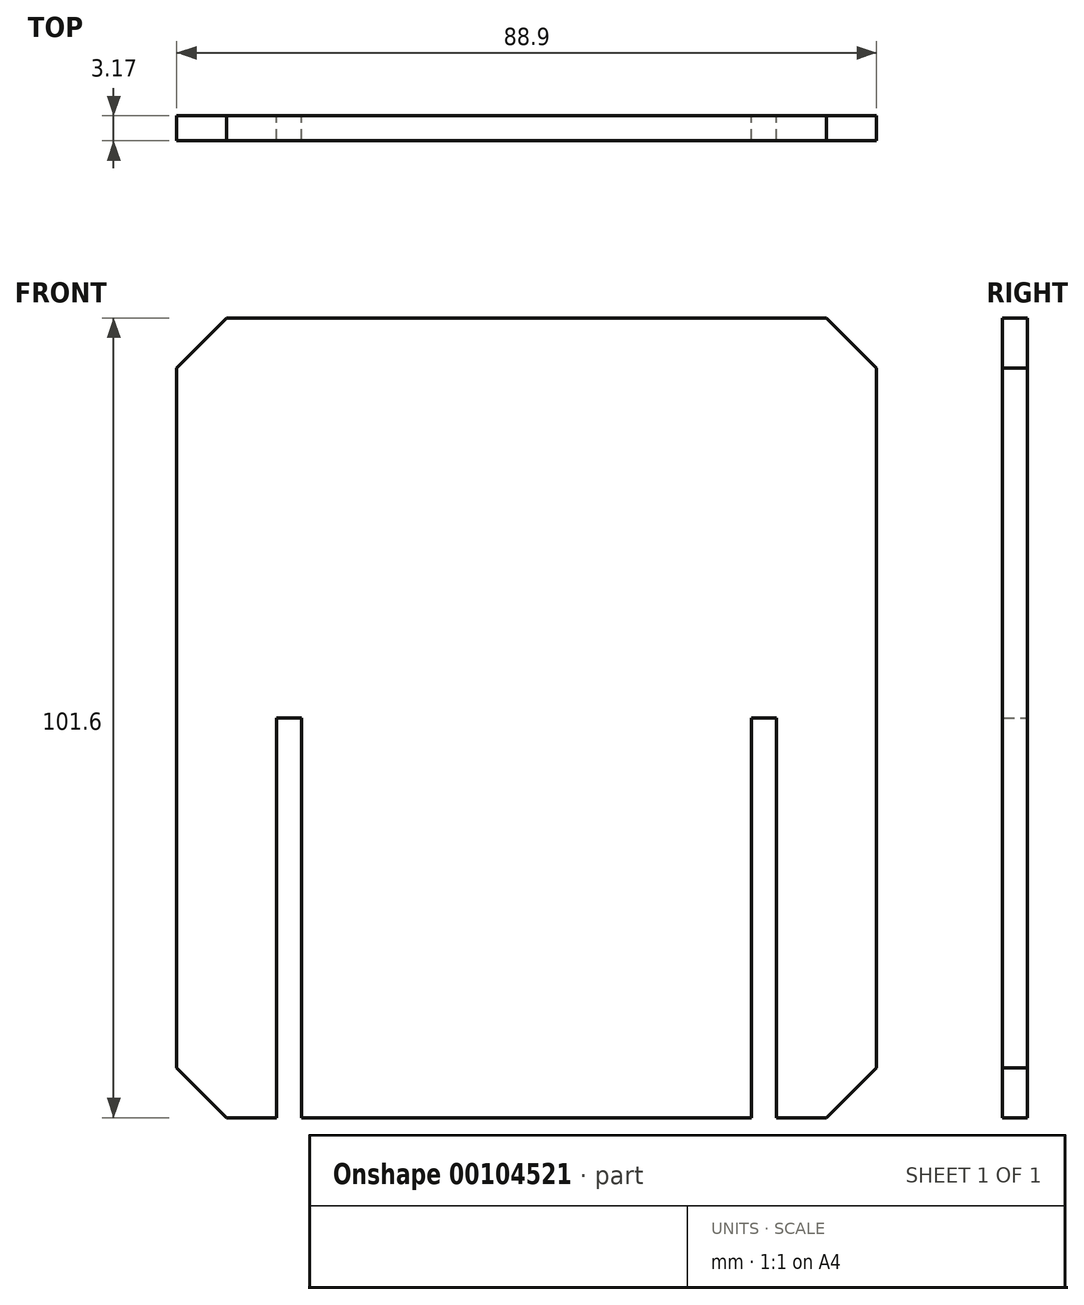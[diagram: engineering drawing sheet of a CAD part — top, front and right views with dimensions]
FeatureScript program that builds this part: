
annotation { "Feature Type Name" : "Feature", "Feature Type Description" : "" }
export const myFeature = defineFeature(function(context is Context, id is Id, definition is map)
    precondition{}
    {
        {
            var Q0;
            Q0=qCreatedBy(makeId("Front.planeOp"),FACE);
            var sketch = newSketch(context, id + "F0", { "sketchPlane" : qUnion([Q0])});
            skLineSegment(sketch, "E0.bottom", {"start": v(6.35, 0) * mm, "end": v(12.7, 0) * mm});
            skLineSegment(sketch, "E0.top", {"start": v(6.35, 101.6) * mm, "end": v(82.55, 101.6) * mm});
            skLineSegment(sketch, "E0.left", {"start": v(0, 6.35) * mm, "end": v(0, 95.25) * mm});
            skLineSegment(sketch, "E0.right", {"start": v(88.9, 6.35) * mm, "end": v(88.9, 95.25) * mm});
            skLineSegment(sketch, "E1.top", {"start": v(12.7, 50.8) * mm, "end": v(15.87, 50.8) * mm});
            skLineSegment(sketch, "E1.left", {"start": v(12.7, 0) * mm, "end": v(12.7, 50.8) * mm});
            skLineSegment(sketch, "E1.right", {"start": v(15.88, 0) * mm, "end": v(15.87, 50.8) * mm});
            skLineSegment(sketch, "E2.top", {"start": v(73.02, 50.8) * mm, "end": v(76.2, 50.8) * mm});
            skLineSegment(sketch, "E2.left", {"start": v(73.02, 0) * mm, "end": v(73.02, 50.8) * mm});
            skLineSegment(sketch, "E2.right", {"start": v(76.2, 0) * mm, "end": v(76.2, 50.8) * mm});
            skLineSegment(sketch, "E3.trimOffspring", {"start": v(15.88, 0) * mm, "end": v(73.02, 0) * mm});
            skLineSegment(sketch, "E4.trimOffspring", {"start": v(76.2, 0) * mm, "end": v(82.55, 0) * mm});
            skLineSegment(sketch, "E5", {"start": v(6.35, 0) * mm, "end": v(0, 6.35) * mm});
            skLineSegment(sketch, "E6", {"start": v(82.55, 0) * mm, "end": v(88.9, 6.35) * mm});
            skLineSegment(sketch, "E7", {"start": v(88.9, 95.25) * mm, "end": v(82.55, 101.6) * mm});
            skLineSegment(sketch, "E8", {"start": v(0, 95.25) * mm, "end": v(6.35, 101.6) * mm});
            skPoint(sketch, "E9.orphan", {"position": v(88.9, 0) * mm});
            skPoint(sketch, "E10.orphan", {"position": v(0, 0) * mm});
            skSolve(sketch);
        }
        {
            var Q0;
            Q0 = qSketchRegion(id + "F0", true);
            extrude(context, id + "F1", {"entities" : qUnion([Q0]), "depth" : 3.17 * mm});
        }
    });
